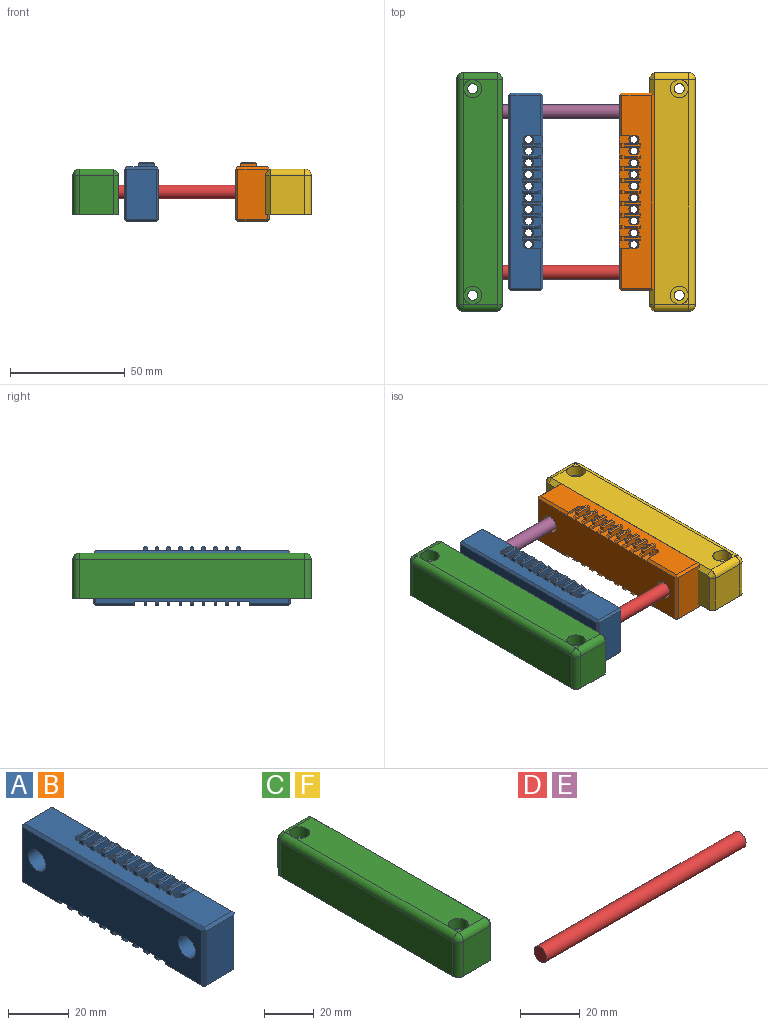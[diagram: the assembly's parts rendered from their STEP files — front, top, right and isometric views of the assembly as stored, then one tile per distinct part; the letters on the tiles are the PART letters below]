
ASSEMBLY  parts=6 mates=5
PART A: 246 faces, bbox 15x86x26 mm
  f0: plane 1.68x1mm, normal (0,0,1), area 1.7mm2, adj f32,f33,f114,f175
  f1: plane 84x13mm, normal (0,0,1), area 728.4mm2, adj f31,f32,f33,f34,f35,f36,f37,f38
  f2: plane 1.68x1mm, normal (0,0,1), area 1.7mm2, adj f34,f54,f113,f172
  f3: plane 1.68x1mm, normal (0,0,1), area 1.7mm2, adj f35,f36,f112,f169
  f4: plane 1.68x1mm, normal (0,0,1), area 1.7mm2, adj f37,f59,f111,f166
  f5: plane 1.68x1mm, normal (0,0,1), area 1.7mm2, adj f38,f39,f110,f163
  f6: plane 1.68x1mm, normal (0,0,1), area 1.7mm2, adj f40,f64,f109,f160
  f7: plane 1.68x1mm, normal (0,0,1), area 1.7mm2, adj f41,f42,f108,f157
  f8: plane 1.68x1mm, normal (0,0,1), area 1.7mm2, adj f43,f69,f107,f154
  f9: plane 1.68x1mm, normal (0,0,1), area 1.7mm2, adj f44,f45,f106,f151
  f10: plane 84x22mm, normal (1,0,0), area 1707.5mm2, adj f48,f49,f96,f97,f98,f99,f100,f101
  f11: cylinder r=1.7mm len=12.5mm, axis (0,0,1), area 133.5mm2, adj f75,f79,f150
  f12: cylinder r=1.7mm len=12.5mm, axis (0,0,1), area 133.5mm2, adj f72,f77,f147
  f13: cylinder r=1.7mm len=12.5mm, axis (0,0,1), area 133.5mm2, adj f70,f83,f144
  f14: cylinder r=1.7mm len=12.5mm, axis (0,0,1), area 133.5mm2, adj f67,f81,f141
  f15: cylinder r=1.7mm len=12.5mm, axis (0,0,1), area 133.5mm2, adj f65,f87,f138
  f16: cylinder r=1.7mm len=12.5mm, axis (0,0,1), area 133.5mm2, adj f62,f85,f135
  f17: cylinder r=1.7mm len=12.5mm, axis (0,0,1), area 133.5mm2, adj f60,f91,f132
  f18: cylinder r=1.7mm len=12.5mm, axis (0,0,1), area 133.5mm2, adj f57,f89,f129
  f19: cylinder r=1.7mm len=12.5mm, axis (0,0,1), area 133.5mm2, adj f55,f95,f126
  f20: cylinder r=1.7mm len=12.5mm, axis (0,0,1), area 133.5mm2, adj f52,f93,f123
  f21: plane 17.14x13mm, normal (0,0,-1), area 222.8mm2, adj f149,f233,f236,f238
  f22: plane 13x1.08mm, normal (0,0,-1), area 14mm2, adj f146,f148,f214,f231
  f23: plane 13x1.08mm, normal (0,0,-1), area 14mm2, adj f143,f145,f215,f230
  f24: plane 13x1.08mm, normal (0,0,-1), area 14mm2, adj f140,f142,f216,f229
  f25: plane 13x1.08mm, normal (0,0,-1), area 14mm2, adj f137,f139,f217,f228
  f26: plane 13x1.08mm, normal (0,0,-1), area 14mm2, adj f134,f136,f218,f227
  f27: plane 13x1.08mm, normal (0,0,-1), area 14mm2, adj f131,f133,f219,f226
  f28: plane 13x1.08mm, normal (0,0,-1), area 14mm2, adj f128,f130,f220,f225
  f29: plane 13x1.08mm, normal (0,0,-1), area 14mm2, adj f125,f127,f221,f224
  f30: plane 13x1.08mm, normal (0,0,-1), area 14mm2, adj f122,f124,f222,f223
  f31: plane 9.5x6.8mm, normal (0,1,0), area 14.8mm2, adj f1,f51,f52,f92,f93,f105,f115
  f32: plane 11x9mm, normal (0,-1,0), area 25.3mm2, adj f0,f1,f51,f52,f92,f93,f105,f114
  f33: plane 11x9mm, normal (0,1,0), area 25.3mm2, adj f0,f1,f53,f55,f94,f95,f96,f114
  f34: plane 11x9mm, normal (0,1,0), area 25.3mm2, adj f1,f2,f56,f57,f88,f89,f104,f113
  f35: plane 11x9mm, normal (0,-1,0), area 25.3mm2, adj f1,f3,f56,f57,f88,f89,f104,f112
  f36: plane 11x9mm, normal (0,1,0), area 25.3mm2, adj f1,f3,f58,f60,f90,f91,f97,f112
  f37: plane 11x9mm, normal (0,1,0), area 25.3mm2, adj f1,f4,f61,f62,f84,f85,f103,f111
  f38: plane 11x9mm, normal (0,-1,0), area 25.3mm2, adj f1,f5,f61,f62,f84,f85,f103,f110
  f39: plane 11x9mm, normal (0,1,0), area 25.3mm2, adj f1,f5,f63,f65,f86,f87,f98,f110
  f40: plane 11x9mm, normal (0,1,0), area 25.3mm2, adj f1,f6,f66,f67,f80,f81,f102,f109
  f41: plane 11x9mm, normal (0,-1,0), area 25.3mm2, adj f1,f7,f66,f67,f80,f81,f102,f108
  f42: plane 11x9mm, normal (0,1,0), area 25.3mm2, adj f1,f7,f68,f70,f82,f83,f99,f108
  f43: plane 11x9mm, normal (0,1,0), area 25.3mm2, adj f1,f8,f71,f72,f76,f77,f101,f107
  f44: plane 11x9mm, normal (0,-1,0), area 25.3mm2, adj f1,f9,f71,f72,f76,f77,f101,f106
  f45: plane 11x9mm, normal (0,1,0), area 25.3mm2, adj f1,f9,f73,f75,f78,f79,f100,f106
  f46: plane 84x22mm, normal (-1,0,0), area 1707.5mm2, adj f48,f49,f118,f121,f122,f123,f124,f125
  f47: plane 22x13mm, normal (0,-1,0), area 286mm2, adj f116,f239,f242,f243
  f48: cylinder r=4mm len=15mm, axis (-1,0,0), area 377mm2, adj f10,f46
  f49: cylinder r=4mm len=15mm, axis (-1,0,0), area 377mm2, adj f10,f46
  f50: plane 22x13mm, normal (0,1,0), area 286mm2, adj f119,f232,f235,f236
  f51: cylinder r=1.7mm len=8.5mm, axis (0,0,1), area 45.4mm2, adj f31,f32,f52,f105
  f52: plane 3.4x2.2mm, normal (0,0,1), area 1.7mm2, adj f20,f31,f32,f51
  f53: cylinder r=1.7mm len=9.5mm, axis (0,0,1), area 50.7mm2, adj f1,f33,f54,f55
  f54: plane 11x9mm, normal (0,-1,0), area 25.3mm2, adj f1,f2,f53,f55,f94,f95,f96,f113
  f55: plane 3.4x2.2mm, normal (0,0,1), area 1.7mm2, adj f19,f33,f53,f54
  f56: cylinder r=1.7mm len=8.5mm, axis (0,0,1), area 45.4mm2, adj f34,f35,f57,f104
  f57: plane 3.4x2.2mm, normal (0,0,1), area 1.7mm2, adj f18,f34,f35,f56
  f58: cylinder r=1.7mm len=9.5mm, axis (0,0,1), area 50.7mm2, adj f1,f36,f59,f60
  f59: plane 11x9mm, normal (0,-1,0), area 25.3mm2, adj f1,f4,f58,f60,f90,f91,f97,f111
  f60: plane 3.4x2.2mm, normal (0,0,1), area 1.7mm2, adj f17,f36,f58,f59
  f61: cylinder r=1.7mm len=8.5mm, axis (0,0,1), area 45.4mm2, adj f37,f38,f62,f103
  f62: plane 3.4x2.2mm, normal (0,0,1), area 1.7mm2, adj f16,f37,f38,f61
  f63: cylinder r=1.7mm len=9.5mm, axis (0,0,1), area 50.7mm2, adj f1,f39,f64,f65
  f64: plane 11x9mm, normal (0,-1,0), area 25.3mm2, adj f1,f6,f63,f65,f86,f87,f98,f109
  f65: plane 3.4x2.2mm, normal (0,0,1), area 1.7mm2, adj f15,f39,f63,f64
  f66: cylinder r=1.7mm len=8.5mm, axis (0,0,1), area 45.4mm2, adj f40,f41,f67,f102
  f67: plane 3.4x2.2mm, normal (0,0,1), area 1.7mm2, adj f14,f40,f41,f66
  f68: cylinder r=1.7mm len=9.5mm, axis (0,0,1), area 50.7mm2, adj f1,f42,f69,f70
  f69: plane 11x9mm, normal (0,-1,0), area 25.3mm2, adj f1,f8,f68,f70,f82,f83,f99,f107
  f70: plane 3.4x2.2mm, normal (0,0,1), area 1.7mm2, adj f13,f42,f68,f69
  f71: cylinder r=1.7mm len=8.5mm, axis (0,0,1), area 45.4mm2, adj f43,f44,f72,f101
  f72: plane 3.4x2.2mm, normal (0,0,1), area 1.7mm2, adj f12,f43,f44,f71
  f73: cylinder r=1.7mm len=9.5mm, axis (0,0,1), area 50.7mm2, adj f1,f45,f74,f75
  f74: plane 9.5x6.8mm, normal (0,-1,0), area 14.8mm2, adj f1,f73,f75,f78,f79,f100,f117
  f75: plane 3.4x2.2mm, normal (0,0,1), area 1.7mm2, adj f11,f45,f73,f74
  f76: cylinder r=1.7mm len=9.5mm, axis (0,0,1), area 50.7mm2, adj f1,f43,f44,f77
  f77: plane 3.4x2.2mm, normal (0,0,1), area 1.7mm2, adj f12,f43,f44,f76
  f78: cylinder r=1.7mm len=8.5mm, axis (0,0,1), area 45.4mm2, adj f45,f74,f79,f100
  f79: plane 3.4x2.2mm, normal (0,0,1), area 1.7mm2, adj f11,f45,f74,f78
  f80: cylinder r=1.7mm len=9.5mm, axis (0,0,1), area 50.7mm2, adj f1,f40,f41,f81
  f81: plane 3.4x2.2mm, normal (0,0,1), area 1.7mm2, adj f14,f40,f41,f80
  f82: cylinder r=1.7mm len=8.5mm, axis (0,0,1), area 45.4mm2, adj f42,f69,f83,f99
  f83: plane 3.4x2.2mm, normal (0,0,1), area 1.7mm2, adj f13,f42,f69,f82
  f84: cylinder r=1.7mm len=9.5mm, axis (0,0,1), area 50.7mm2, adj f1,f37,f38,f85
  f85: plane 3.4x2.2mm, normal (0,0,1), area 1.7mm2, adj f16,f37,f38,f84
  f86: cylinder r=1.7mm len=8.5mm, axis (0,0,1), area 45.4mm2, adj f39,f64,f87,f98
  f87: plane 3.4x2.2mm, normal (0,0,1), area 1.7mm2, adj f15,f39,f64,f86
  f88: cylinder r=1.7mm len=9.5mm, axis (0,0,1), area 50.7mm2, adj f1,f34,f35,f89
  f89: plane 3.4x2.2mm, normal (0,0,1), area 1.7mm2, adj f18,f34,f35,f88
  f90: cylinder r=1.7mm len=8.5mm, axis (0,0,1), area 45.4mm2, adj f36,f59,f91,f97
  f91: plane 3.4x2.2mm, normal (0,0,1), area 1.7mm2, adj f17,f36,f59,f90
  f92: cylinder r=1.7mm len=9.5mm, axis (0,0,1), area 50.7mm2, adj f1,f31,f32,f93
  f93: plane 3.4x2.2mm, normal (0,0,1), area 1.7mm2, adj f20,f31,f32,f92
  f94: cylinder r=1.7mm len=8.5mm, axis (0,0,1), area 45.4mm2, adj f33,f54,f95,f96
  f95: plane 3.4x2.2mm, normal (0,0,1), area 1.7mm2, adj f19,f33,f54,f94
  f96: plane 5.8x3.4mm, normal (0,0,1), area 15.2mm2, adj f10,f33,f54,f94
  f97: plane 5.8x3.4mm, normal (0,0,1), area 15.2mm2, adj f10,f36,f59,f90
  f98: plane 5.8x3.4mm, normal (0,0,1), area 15.2mm2, adj f10,f39,f64,f86
  f99: plane 5.8x3.4mm, normal (0,0,1), area 15.2mm2, adj f10,f42,f69,f82
  f100: plane 5.8x3.4mm, normal (0,0,1), area 15.2mm2, adj f10,f45,f74,f78
  f101: plane 5.8x3.4mm, normal (0,0,1), area 15.2mm2, adj f10,f43,f44,f71
  f102: plane 5.8x3.4mm, normal (0,0,1), area 15.2mm2, adj f10,f40,f41,f66
  f103: plane 5.8x3.4mm, normal (0,0,1), area 15.2mm2, adj f10,f37,f38,f61
  f104: plane 5.8x3.4mm, normal (0,0,1), area 15.2mm2, adj f10,f34,f35,f56
  f105: plane 5.8x3.4mm, normal (0,0,1), area 15.2mm2, adj f10,f31,f32,f51
  f106: plane 1.68x1mm, normal (0.71,0,0.71), area 2.4mm2, adj f9,f10,f44,f45
  f107: plane 1.68x1mm, normal (0.71,0,0.71), area 2.4mm2, adj f8,f10,f43,f69
  f108: plane 1.68x1mm, normal (0.71,0,0.71), area 2.4mm2, adj f7,f10,f41,f42
  f109: plane 1.68x1mm, normal (0.71,0,0.71), area 2.4mm2, adj f6,f10,f40,f64
  f110: plane 1.68x1mm, normal (0.71,0,0.71), area 2.4mm2, adj f5,f10,f38,f39
  f111: plane 1.68x1mm, normal (0.71,0,0.71), area 2.4mm2, adj f4,f10,f37,f59
  f112: plane 1.68x1mm, normal (0.71,0,0.71), area 2.4mm2, adj f3,f10,f35,f36
  f113: plane 1.68x1mm, normal (0.71,0,0.71), area 2.4mm2, adj f2,f10,f34,f54
  f114: plane 1.68x1mm, normal (0.71,0,0.71), area 2.4mm2, adj f0,f10,f32,f33
  f115: plane 17.94x1mm, normal (0.71,0,0.71), area 25mm2, adj f1,f10,f31,f116,f239
  f116: plane 14x1mm, normal (0,-0.71,0.71), area 19.1mm2, adj f1,f47,f115,f118,f239,f242
  f117: plane 17.94x1mm, normal (0.71,0,0.71), area 25mm2, adj f1,f10,f74,f119,f235
  f118: plane 85x1mm, normal (-0.71,0,0.71), area 119.5mm2, adj f1,f46,f116,f119,f232,f242
  f119: plane 14x1mm, normal (0,0.71,0.71), area 19.1mm2, adj f1,f50,f117,f118,f232,f235
  f120: plane 17.14x13mm, normal (0,0,-1), area 222.8mm2, adj f121,f240,f243,f245
  f121: plane 15x2mm, normal (0,1,0), area 29mm2, adj f10,f46,f120,f123,f240,f245
  f122: plane 15x2mm, normal (0,-1,0), area 29mm2, adj f10,f30,f46,f123,f222,f223
  f123: plane 15x4mm, normal (0,0,-1), area 50.9mm2, adj f10,f20,f46,f121,f122
  f124: plane 15x2mm, normal (0,1,0), area 29mm2, adj f10,f30,f46,f126,f222,f223
  f125: plane 15x2mm, normal (0,-1,0), area 29mm2, adj f10,f29,f46,f126,f221,f224
  f126: plane 15x4mm, normal (0,0,-1), area 50.9mm2, adj f10,f19,f46,f124,f125
  f127: plane 15x2mm, normal (0,1,0), area 29mm2, adj f10,f29,f46,f129,f221,f224
  f128: plane 15x2mm, normal (0,-1,0), area 29mm2, adj f10,f28,f46,f129,f220,f225
  f129: plane 15x4mm, normal (0,0,-1), area 50.9mm2, adj f10,f18,f46,f127,f128
  f130: plane 15x2mm, normal (0,1,0), area 29mm2, adj f10,f28,f46,f132,f220,f225
  f131: plane 15x2mm, normal (0,-1,0), area 29mm2, adj f10,f27,f46,f132,f219,f226
  f132: plane 15x4mm, normal (0,0,-1), area 50.9mm2, adj f10,f17,f46,f130,f131
  f133: plane 15x2mm, normal (0,1,0), area 29mm2, adj f10,f27,f46,f135,f219,f226
  f134: plane 15x2mm, normal (0,-1,0), area 29mm2, adj f10,f26,f46,f135,f218,f227
  f135: plane 15x4mm, normal (0,0,-1), area 50.9mm2, adj f10,f16,f46,f133,f134
  f136: plane 15x2mm, normal (0,1,0), area 29mm2, adj f10,f26,f46,f138,f218,f227
  f137: plane 15x2mm, normal (0,-1,0), area 29mm2, adj f10,f25,f46,f138,f217,f228
  f138: plane 15x4mm, normal (0,0,-1), area 50.9mm2, adj f10,f15,f46,f136,f137
  f139: plane 15x2mm, normal (0,1,0), area 29mm2, adj f10,f25,f46,f141,f217,f228
  f140: plane 15x2mm, normal (0,-1,0), area 29mm2, adj f10,f24,f46,f141,f216,f229
  f141: plane 15x4mm, normal (0,0,-1), area 50.9mm2, adj f10,f14,f46,f139,f140
  f142: plane 15x2mm, normal (0,1,0), area 29mm2, adj f10,f24,f46,f144,f216,f229
  f143: plane 15x2mm, normal (0,-1,0), area 29mm2, adj f10,f23,f46,f144,f215,f230
  f144: plane 15x4mm, normal (0,0,-1), area 50.9mm2, adj f10,f13,f46,f142,f143
  f145: plane 15x2mm, normal (0,1,0), area 29mm2, adj f10,f23,f46,f147,f215,f230
  f146: plane 15x2mm, normal (0,-1,0), area 29mm2, adj f10,f22,f46,f147,f214,f231
  f147: plane 15x4mm, normal (0,0,-1), area 50.9mm2, adj f10,f12,f46,f145,f146
  f148: plane 15x2mm, normal (0,1,0), area 29mm2, adj f10,f22,f46,f150,f214,f231
  f149: plane 15x2mm, normal (0,-1,0), area 29mm2, adj f10,f21,f46,f150,f233,f238
  f150: plane 15x4mm, normal (0,0,-1), area 50.9mm2, adj f10,f11,f46,f148,f149
  f151: plane 1.68x1.5mm, normal (1,0,0), area 2.5mm2, adj f9,f44,f45,f178
  f152: plane 1.68x1.5mm, normal (-1,0,0), area 2.5mm2, adj f1,f44,f45,f181
  f153: plane 6x0.68mm, normal (0,0,1), area 4.1mm2, adj f178,f179,f180,f181
  f154: plane 1.68x1.5mm, normal (1,0,0), area 2.5mm2, adj f8,f43,f69,f182
  f155: plane 1.68x1.5mm, normal (-1,0,0), area 2.5mm2, adj f1,f43,f69,f185
  f156: plane 6x0.68mm, normal (0,0,1), area 4.1mm2, adj f182,f183,f184,f185
  f157: plane 1.68x1.5mm, normal (1,0,0), area 2.5mm2, adj f7,f41,f42,f186
  f158: plane 1.68x1.5mm, normal (-1,0,0), area 2.5mm2, adj f1,f41,f42,f189
  f159: plane 6x0.68mm, normal (0,0,1), area 4.1mm2, adj f186,f187,f188,f189
  f160: plane 1.68x1.5mm, normal (1,0,0), area 2.5mm2, adj f6,f40,f64,f190
  f161: plane 1.68x1.5mm, normal (-1,0,0), area 2.5mm2, adj f1,f40,f64,f193
  f162: plane 6x0.68mm, normal (0,0,1), area 4.1mm2, adj f190,f191,f192,f193
  f163: plane 1.68x1.5mm, normal (1,0,0), area 2.5mm2, adj f5,f38,f39,f194
  f164: plane 1.68x1.5mm, normal (-1,0,0), area 2.5mm2, adj f1,f38,f39,f197
  f165: plane 6x0.68mm, normal (0,0,1), area 4.1mm2, adj f194,f195,f196,f197
  f166: plane 1.68x1.5mm, normal (1,0,0), area 2.5mm2, adj f4,f37,f59,f198
  f167: plane 1.68x1.5mm, normal (-1,0,0), area 2.5mm2, adj f1,f37,f59,f201
  f168: plane 6x0.68mm, normal (0,0,1), area 4.1mm2, adj f198,f199,f200,f201
  f169: plane 1.68x1.5mm, normal (1,0,0), area 2.5mm2, adj f3,f35,f36,f202
  f170: plane 1.68x1.5mm, normal (-1,0,0), area 2.5mm2, adj f1,f35,f36,f205
  f171: plane 6x0.68mm, normal (0,0,1), area 4.1mm2, adj f202,f203,f204,f205
  f172: plane 1.68x1.5mm, normal (1,0,0), area 2.5mm2, adj f2,f34,f54,f206
  f173: plane 1.68x1.5mm, normal (-1,0,0), area 2.5mm2, adj f1,f34,f54,f209
  f174: plane 6x0.68mm, normal (0,0,1), area 4.1mm2, adj f206,f207,f208,f209
  f175: plane 1.68x1.5mm, normal (1,0,0), area 2.5mm2, adj f0,f32,f33,f210
  f176: plane 1.68x1.5mm, normal (-1,0,0), area 2.5mm2, adj f1,f32,f33,f213
  f177: plane 6x0.68mm, normal (0,0,1), area 4.1mm2, adj f210,f211,f212,f213
  f178: plane 1.68x0.5mm, normal (0.71,0,0.71), area 0.8mm2, adj f151,f153,f179,f180
  f179: plane 7x0.5mm, normal (0,0.71,0.71), area 4.6mm2, adj f45,f153,f178,f181
  f180: plane 7x0.5mm, normal (0,-0.71,0.71), area 4.6mm2, adj f44,f153,f178,f181
  f181: plane 1.68x0.5mm, normal (-0.71,0,0.71), area 0.8mm2, adj f152,f153,f179,f180
  f182: plane 1.68x0.5mm, normal (0.71,0,0.71), area 0.8mm2, adj f154,f156,f183,f184
  f183: plane 7x0.5mm, normal (0,0.71,0.71), area 4.6mm2, adj f43,f156,f182,f185
  f184: plane 7x0.5mm, normal (0,-0.71,0.71), area 4.6mm2, adj f69,f156,f182,f185
  f185: plane 1.68x0.5mm, normal (-0.71,0,0.71), area 0.8mm2, adj f155,f156,f183,f184
  f186: plane 1.68x0.5mm, normal (0.71,0,0.71), area 0.8mm2, adj f157,f159,f187,f188
  f187: plane 7x0.5mm, normal (0,0.71,0.71), area 4.6mm2, adj f42,f159,f186,f189
  f188: plane 7x0.5mm, normal (0,-0.71,0.71), area 4.6mm2, adj f41,f159,f186,f189
  f189: plane 1.68x0.5mm, normal (-0.71,0,0.71), area 0.8mm2, adj f158,f159,f187,f188
  f190: plane 1.68x0.5mm, normal (0.71,0,0.71), area 0.8mm2, adj f160,f162,f191,f192
  f191: plane 7x0.5mm, normal (0,0.71,0.71), area 4.6mm2, adj f40,f162,f190,f193
  f192: plane 7x0.5mm, normal (0,-0.71,0.71), area 4.6mm2, adj f64,f162,f190,f193
  f193: plane 1.68x0.5mm, normal (-0.71,0,0.71), area 0.8mm2, adj f161,f162,f191,f192
  f194: plane 1.68x0.5mm, normal (0.71,0,0.71), area 0.8mm2, adj f163,f165,f195,f196
  f195: plane 7x0.5mm, normal (0,0.71,0.71), area 4.6mm2, adj f39,f165,f194,f197
  f196: plane 7x0.5mm, normal (0,-0.71,0.71), area 4.6mm2, adj f38,f165,f194,f197
  f197: plane 1.68x0.5mm, normal (-0.71,0,0.71), area 0.8mm2, adj f164,f165,f195,f196
  f198: plane 1.68x0.5mm, normal (0.71,0,0.71), area 0.8mm2, adj f166,f168,f199,f200
  f199: plane 7x0.5mm, normal (0,0.71,0.71), area 4.6mm2, adj f37,f168,f198,f201
  f200: plane 7x0.5mm, normal (0,-0.71,0.71), area 4.6mm2, adj f59,f168,f198,f201
  f201: plane 1.68x0.5mm, normal (-0.71,0,0.71), area 0.8mm2, adj f167,f168,f199,f200
  f202: plane 1.68x0.5mm, normal (0.71,0,0.71), area 0.8mm2, adj f169,f171,f203,f204
  f203: plane 7x0.5mm, normal (0,0.71,0.71), area 4.6mm2, adj f36,f171,f202,f205
  f204: plane 7x0.5mm, normal (0,-0.71,0.71), area 4.6mm2, adj f35,f171,f202,f205
  f205: plane 1.68x0.5mm, normal (-0.71,0,0.71), area 0.8mm2, adj f170,f171,f203,f204
  f206: plane 1.68x0.5mm, normal (0.71,0,0.71), area 0.8mm2, adj f172,f174,f207,f208
  f207: plane 7x0.5mm, normal (0,0.71,0.71), area 4.6mm2, adj f34,f174,f206,f209
  f208: plane 7x0.5mm, normal (0,-0.71,0.71), area 4.6mm2, adj f54,f174,f206,f209
  f209: plane 1.68x0.5mm, normal (-0.71,0,0.71), area 0.8mm2, adj f173,f174,f207,f208
  f210: plane 1.68x0.5mm, normal (0.71,0,0.71), area 0.8mm2, adj f175,f177,f211,f212
  f211: plane 7x0.5mm, normal (0,0.71,0.71), area 4.6mm2, adj f33,f177,f210,f213
  f212: plane 7x0.5mm, normal (0,-0.71,0.71), area 4.6mm2, adj f32,f177,f210,f213
  f213: plane 1.68x0.5mm, normal (-0.71,0,0.71), area 0.8mm2, adj f176,f177,f211,f212
  f214: plane 1.08x1mm, normal (0.71,0,-0.71), area 1.5mm2, adj f10,f22,f146,f148
  f215: plane 1.08x1mm, normal (0.71,0,-0.71), area 1.5mm2, adj f10,f23,f143,f145
  f216: plane 1.08x1mm, normal (0.71,0,-0.71), area 1.5mm2, adj f10,f24,f140,f142
  f217: plane 1.08x1mm, normal (0.71,0,-0.71), area 1.5mm2, adj f10,f25,f137,f139
  f218: plane 1.08x1mm, normal (0.71,0,-0.71), area 1.5mm2, adj f10,f26,f134,f136
  f219: plane 1.08x1mm, normal (0.71,0,-0.71), area 1.5mm2, adj f10,f27,f131,f133
  f220: plane 1.08x1mm, normal (0.71,0,-0.71), area 1.5mm2, adj f10,f28,f128,f130
  f221: plane 1.08x1mm, normal (0.71,0,-0.71), area 1.5mm2, adj f10,f29,f125,f127
  f222: plane 1.08x1mm, normal (0.71,0,-0.71), area 1.5mm2, adj f10,f30,f122,f124
  f223: plane 1.08x1mm, normal (-0.71,0,-0.71), area 1.5mm2, adj f30,f46,f122,f124
  f224: plane 1.08x1mm, normal (-0.71,0,-0.71), area 1.5mm2, adj f29,f46,f125,f127
  f225: plane 1.08x1mm, normal (-0.71,0,-0.71), area 1.5mm2, adj f28,f46,f128,f130
  f226: plane 1.08x1mm, normal (-0.71,0,-0.71), area 1.5mm2, adj f27,f46,f131,f133
  f227: plane 1.08x1mm, normal (-0.71,0,-0.71), area 1.5mm2, adj f26,f46,f134,f136
  f228: plane 1.08x1mm, normal (-0.71,0,-0.71), area 1.5mm2, adj f25,f46,f137,f139
  f229: plane 1.08x1mm, normal (-0.71,0,-0.71), area 1.5mm2, adj f24,f46,f140,f142
  f230: plane 1.08x1mm, normal (-0.71,0,-0.71), area 1.5mm2, adj f23,f46,f143,f145
  f231: plane 1.08x1mm, normal (-0.71,0,-0.71), area 1.5mm2, adj f22,f46,f146,f148
  f232: plane 22.5x1mm, normal (-0.71,0.71,0), area 31.5mm2, adj f46,f50,f118,f119,f234
  f233: plane 17.14x1mm, normal (-0.71,0,-0.71), area 24.2mm2, adj f21,f46,f149,f234
  f234: plane 1x1mm, normal (-0.58,0.58,-0.58), area 0.9mm2, adj f232,f233,f236
  f235: plane 22.5x1mm, normal (0.71,0.71,0), area 31.5mm2, adj f10,f50,f117,f119,f237
  f236: plane 13x1mm, normal (0,0.71,-0.71), area 18.4mm2, adj f21,f50,f234,f237
  f237: plane 1x1mm, normal (0.58,0.58,-0.58), area 0.9mm2, adj f235,f236,f238
  f238: plane 17.14x1mm, normal (0.71,0,-0.71), area 24.2mm2, adj f10,f21,f149,f237
  f239: plane 22.5x1mm, normal (0.71,-0.71,0), area 31.5mm2, adj f10,f47,f115,f116,f241
  f240: plane 17.14x1mm, normal (0.71,0,-0.71), area 24.2mm2, adj f10,f120,f121,f241
  f241: plane 1x1mm, normal (0.58,-0.58,-0.58), area 0.9mm2, adj f239,f240,f243
  f242: plane 22.5x1mm, normal (-0.71,-0.71,0), area 31.5mm2, adj f46,f47,f116,f118,f244
  f243: plane 13x1mm, normal (0,-0.71,-0.71), area 18.4mm2, adj f47,f120,f241,f244
  f244: plane 1x1mm, normal (-0.58,-0.58,-0.58), area 0.9mm2, adj f242,f243,f245
  f245: plane 17.14x1mm, normal (-0.71,0,-0.71), area 24.2mm2, adj f46,f120,f121,f244
PART B: same geometry as A
PART C: 30 faces, bbox 20x104x20 mm
  f0: plane 4x4mm, normal (0,0,1), area 3.4mm2, adj f14,f16,f22
  f1: plane 98x15mm, normal (0,0,1), area 1362.6mm2, adj f14,f15,f16,f18,f22,f27
  f2: cylinder r=2.2mm len=15mm, axis (0,0,1), area 207.3mm2, adj f6,f19
  f3: cylinder r=2.2mm len=15mm, axis (0,0,1), area 207.3mm2, adj f6,f17
  f4: plane 4x4mm, normal (0,0,1), area 3.4mm2, adj f15,f18,f22
  f5: plane 98x17mm, normal (-1,0,0), area 1666mm2, adj f6,f20,f22,f24
  f6: plane 104x20mm, normal (0,0,-1), area 2041.7mm2, adj f2,f3,f5,f7,f8,f9,f20,f24
  f7: plane 100x18mm, normal (1,0,0), area 1739.2mm2, adj f6,f10,f12,f25,f26,f27,f28,f29
  f8: plane 17x15mm, normal (0,-1,0), area 255mm2, adj f6,f15,f20,f29
  f9: plane 17x15mm, normal (0,1,0), area 255mm2, adj f6,f14,f24,f25
  f10: cylinder r=3.1mm len=15mm, axis (1,0,0), area 292.2mm2, adj f7,f11
  f11: plane 6.2x6.2mm, normal (1,0,0), area 30.2mm2, adj f10
  f12: cylinder r=3.1mm len=15mm, axis (1,0,0), area 292.2mm2, adj f7,f13
  f13: plane 6.2x6.2mm, normal (1,0,0), area 30.2mm2, adj f12
  f14: cylinder r=3mm len=15mm, axis (-1,0,0), area 70.7mm2, adj f0,f1,f9,f23,f26
  f15: cylinder r=3mm len=15mm, axis (1,0,0), area 70.7mm2, adj f1,f4,f8,f21,f28
  f16: cylinder r=4mm len=8mm, axis (0,0,1), area 125.7mm2, adj f0,f1,f17
  f17: plane 8x8mm, normal (0,0,1), area 35.1mm2, adj f3,f16
  f18: cylinder r=4mm len=8mm, axis (0,0,1), area 125.7mm2, adj f1,f4,f19
  f19: plane 8x8mm, normal (0,0,1), area 35.1mm2, adj f2,f18
  f20: cylinder r=3mm len=17mm, axis (0,0,1), area 80.1mm2, adj f5,f6,f8,f21
  f21: sphere r=3mm, area 14.1mm2, adj f15,f20,f22
  f22: cylinder r=3mm len=98mm, axis (0,-1,0), area 461.8mm2, adj f0,f1,f4,f5,f21,f23
  f23: sphere r=3mm, area 14.1mm2, adj f14,f22,f24
  f24: cylinder r=3mm len=17mm, axis (0,0,-1), area 80.1mm2, adj f5,f6,f9,f23
  f25: plane 17x2mm, normal (0.71,0.71,0), area 48.1mm2, adj f6,f7,f9,f26
  f26: cone r=1mm half-angle=45deg, axis (-1,0,0), area 8.9mm2, adj f7,f14,f25,f27
  f27: plane 98x2mm, normal (0.71,0,0.71), area 277.2mm2, adj f1,f7,f26,f28
  f28: cone r=1mm half-angle=45deg, axis (-1,0,0), area 8.9mm2, adj f7,f15,f27,f29
  f29: plane 17x2mm, normal (0.71,-0.71,0), area 48.1mm2, adj f6,f7,f8,f28
PART D: 3 faces, bbox 94x6x6 mm
  f0: cylinder r=3mm len=94mm, axis (-1,0,0), area 1771.9mm2, adj f1,f2
  f1: plane 6x6mm, normal (1,0,0), area 28.3mm2, adj f0
  f2: plane 6x6mm, normal (-1,0,0), area 28.3mm2, adj f0
PART E: same geometry as D
PART F: same geometry as C
PLACE A t=(-39.37,-11.08,-21.12)mm
PLACE B rot(axis=(0,0,1),180deg) t=(23.96,-9.26,-21.12)mm
PLACE C t=(-53.13,41.83,-25.65)mm
PLACE D t=(-56.98,-9.35,-41.68)mm
PLACE E t=(-56.98,60.65,-41.68)mm
PLACE F rot(axis=(0,0,1),180deg) t=(33.17,-62.17,-25.65)mm
MATE fastened D.f0 <-> C.f12  axis (-1,0,0) through (-56.98,-45.17,-20.48)mm
MATE fastened E.f0 <-> C.f10  axis (-1,0,0) through (-56.98,24.83,-20.48)mm
MATE slider B.f49 <-> D.f0  axis (1,0,0) through (23.96,-45.17,-20.48)mm
MATE slider A.f48 <-> D.f0  axis (1,0,0) through (-24.37,-45.17,-20.48)mm
MATE fastened F.f12 <-> E.f0  axis (-1,0,0) through (37.02,24.83,-20.48)mm
